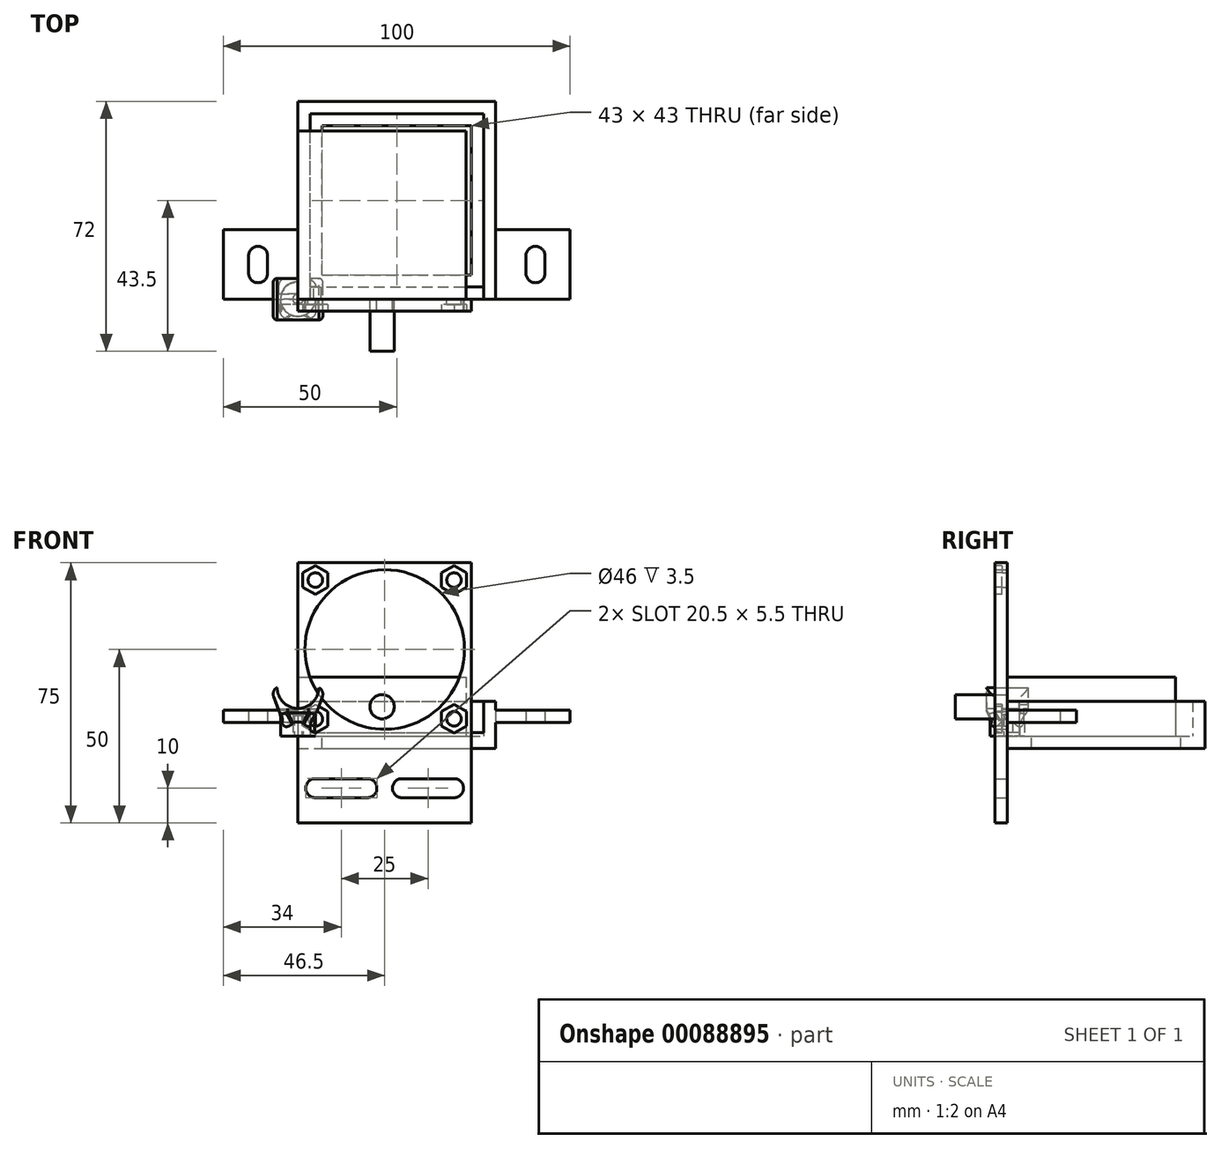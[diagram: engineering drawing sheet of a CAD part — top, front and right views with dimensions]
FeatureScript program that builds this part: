
annotation { "Feature Type Name" : "Feature", "Feature Type Description" : "" }
export const myFeature = defineFeature(function(context is Context, id is Id, definition is map)
    precondition{}
    {
        {
            var Q0;
            Q0=qCreatedBy(makeId("Top.planeOp"),FACE);
            var sketch = newSketch(context, id + "F0", { "sketchPlane" : qUnion([Q0])});
            skCircle(sketch, "E0", {"center": v(0, 0) * mm, "radius": 5 * mm});
            skArc(sketch, "E1", {"start": v(1.12, -1) * mm, "mid": v(0, 1.5) * mm, "end": v(-1.12, -1) * mm});
            skLineSegment(sketch, "E2", {"start": v(-1.12, -1) * mm, "end": v(1.12, -1) * mm});
            skSolve(sketch);
        }
        {
            var Q0;
            Q0 = qSketchRegion(id + "F0", true);
            extrude(context, id + "F1", {"entities" : qUnion([Q0]), "depth" : 6 * mm});
        }
        {
            var Q0;
            Q0=qCreatedBy(makeId("Front.planeOp"),FACE);
            var sketch = newSketch(context, id + "F2", { "sketchPlane" : qUnion([Q0])});
            skArc(sketch, "E3", {"start": v(-6, 14) * mm, "mid": v(0, 8) * mm, "end": v(6, 14) * mm});
            skLineSegment(sketch, "E4", {"start": v(0, 43.04) * mm, "end": v(0, -18.68) * mm, "construction": true});
            skLineSegment(sketch, "E5", {"start": v(8, 14) * mm, "end": v(6, 14) * mm});
            skLineSegment(sketch, "E6.trimOffspring", {"start": v(-6, 14) * mm, "end": v(-8, 14) * mm});
            skLineSegment(sketch, "E7", {"start": v(8, 14) * mm, "end": v(5, 6) * mm});
            skLineSegment(sketch, "E8", {"start": v(5, 6) * mm, "end": v(-5, 6) * mm});
            skLineSegment(sketch, "E9", {"start": v(-5, 6) * mm, "end": v(-8, 14) * mm});
            skSolve(sketch);
        }
        {
            var Q0;
            Q0 = qSketchRegion(id + "F2", true);
            extrude(context, id + "F3", {"entities" : qUnion([Q0]), "operationType" : NewBodyOperationType.ADD, "endBound" : BoundingType.SYMMETRIC, "depth" : 12 * mm});
        }
        {
            var Q0;
            Q0=makeQuery(id+"F3.opExtrude","CAP_EDGE",EDGE,{"disambiguationData":[OSD([sQuery(id+"F2.wireOp",EDGE,"E7")])],"isStart":false});
            var Q1;
            Q1=makeQuery(id+"F3.opExtrude","CAP_EDGE",EDGE,{"disambiguationData":[OSD([sQuery(id+"F2.wireOp",EDGE,"E9")])],"isStart":false});
            var Q2;
            Q2=makeQuery(id+"F3.opExtrude","CAP_EDGE",EDGE,{"disambiguationData":[OSD([sQuery(id+"F2.wireOp",EDGE,"E9")])],"isStart":true});
            var Q3;
            Q3=makeQuery(id+"F3.opExtrude","CAP_EDGE",EDGE,{"disambiguationData":[OSD([sQuery(id+"F2.wireOp",EDGE,"E7")])],"isStart":true});
            var Q4;
            Q4=makeQuery(id+"F3.opExtrude","SWEPT_EDGE",EDGE,{"disambiguationData":[OSD([sQuery(id+"F2.wireOp",EDGE,"E5"),sQuery(id+"F2.wireOp",EDGE,"E7")])]});
            var Q5;
            Q5=makeQuery(id+"F3.opExtrude","SWEPT_EDGE",EDGE,{"disambiguationData":[OSD([sQuery(id+"F2.wireOp",EDGE,"E6.trimOffspring"),sQuery(id+"F2.wireOp",EDGE,"E9")])]});
            var Q6;
            {var subQ0=sQuery(id+"F2.wireOp",EDGE,"E9");var subQ1=sQuery(id+"F2.wireOp",EDGE,"E8");Q6=makeQuery(id+"F3.boolean.opBoolean","SPLIT",EDGE,{"disambiguationData":[TD([makeQuery(id+"F3.opExtrude","CAP_FACE",FACE,{"disambiguationData":[OSD([sQuery(id+"F2.wireOp",EDGE,"E3"),sQuery(id+"F2.wireOp",EDGE,"E5"),sQuery(id+"F2.wireOp",EDGE,"E6.trimOffspring"),sQuery(id+"F2.wireOp",EDGE,"E7"),subQ1,subQ0])],"isStart":false})])],"derivedFrom":makeQuery(id+"F3.opExtrude","SWEPT_EDGE",EDGE,{"disambiguationData":[OSD([subQ1,subQ0])]})});}
            var Q7;
            Q7=makeQuery(id+"F3.opExtrude","CAP_EDGE",EDGE,{"disambiguationData":[OSD([sQuery(id+"F2.wireOp",EDGE,"E8")])],"isStart":true});
            var Q8;
            {var subQ0=sQuery(id+"F2.wireOp",EDGE,"E8");var subQ1=sQuery(id+"F2.wireOp",EDGE,"E7");Q8=makeQuery(id+"F3.boolean.opBoolean","SPLIT",EDGE,{"disambiguationData":[TD([makeQuery(id+"F3.opExtrude","CAP_FACE",FACE,{"disambiguationData":[OSD([sQuery(id+"F2.wireOp",EDGE,"E3"),sQuery(id+"F2.wireOp",EDGE,"E5"),sQuery(id+"F2.wireOp",EDGE,"E6.trimOffspring"),subQ1,subQ0,sQuery(id+"F2.wireOp",EDGE,"E9")])],"isStart":true})])],"derivedFrom":makeQuery(id+"F3.opExtrude","SWEPT_EDGE",EDGE,{"disambiguationData":[OSD([subQ1,subQ0])]})});}
            var Q9;
            {var subQ0=sQuery(id+"F2.wireOp",EDGE,"E8");var subQ1=sQuery(id+"F2.wireOp",EDGE,"E7");Q9=makeQuery(id+"F3.boolean.opBoolean","SPLIT",EDGE,{"disambiguationData":[TD([makeQuery(id+"F3.opExtrude","CAP_FACE",FACE,{"disambiguationData":[OSD([sQuery(id+"F2.wireOp",EDGE,"E3"),sQuery(id+"F2.wireOp",EDGE,"E5"),sQuery(id+"F2.wireOp",EDGE,"E6.trimOffspring"),subQ1,subQ0,sQuery(id+"F2.wireOp",EDGE,"E9")])],"isStart":false})])],"derivedFrom":makeQuery(id+"F3.opExtrude","SWEPT_EDGE",EDGE,{"disambiguationData":[OSD([subQ1,subQ0])]})});}
            var Q10;
            Q10=makeQuery(id+"F3.opExtrude","CAP_EDGE",EDGE,{"disambiguationData":[OSD([sQuery(id+"F2.wireOp",EDGE,"E8")])],"isStart":false});
            fillet(context, id + "F4", {"entities" : qUnion([Q0, Q1, Q2, Q3, Q4, Q5, Q6, Q7, Q8, Q9, Q10]), "radius" : 2 * mm, "tangentPropagation" : true, "allowEdgeOverflow" : false});
        }
        {
            var Q0;
            Q0=makeQuery(id+"F4.opFillet","BLEND_EDGE",EDGE,{"blendedFrom":[makeQuery(id+"F3.opExtrude","CAP_EDGE",EDGE,{"disambiguationData":[OSD([sQuery(id+"F2.wireOp",EDGE,"E8")])],"isStart":false}),makeQuery(id+"F1.opExtrude","SWEPT_FACE",FACE,{"disambiguationData":[OSD([sQuery(id+"F0.wireOp",EDGE,"E0")])]})],"blendedInto":[makeQuery(id+"F1.opExtrude","SWEPT_FACE",FACE,{"disambiguationData":[OSD([sQuery(id+"F0.wireOp",EDGE,"E0")])]})]});
            fillet(context, id + "F5", {"entities" : qUnion([Q0]), "radius" : 5 * mm, "tangentPropagation" : true, "allowEdgeOverflow" : false});
        }
        {
            var Q0;
            Q0=qCreatedBy(makeId("Right.planeOp"),FACE);
            var sketch = newSketch(context, id + "F6", { "sketchPlane" : qUnion([Q0])});
            skLineSegment(sketch, "E10.bottom", {"start": v(-1.5, 7.75) * mm, "end": v(1.5, 7.75) * mm});
            skLineSegment(sketch, "E10.top", {"start": v(-1.5, 6.25) * mm, "end": v(1.5, 6.25) * mm});
            skLineSegment(sketch, "E10.left", {"start": v(-1.5, 7.75) * mm, "end": v(-1.5, 6.25) * mm});
            skLineSegment(sketch, "E10.right", {"start": v(1.5, 7.75) * mm, "end": v(1.5, 6.25) * mm});
            skSolve(sketch);
        }
        {
            var Q0;
            Q0 = qSketchRegion(id + "F6", true);
            extrude(context, id + "F7", {"entities" : qUnion([Q0]), "operationType" : NewBodyOperationType.REMOVE, "endBound" : BoundingType.SYMMETRIC, "depth" : 100 * mm});
        }
        {
            var Q0;
            Q0=qCreatedBy(makeId("Top.planeOp"),FACE);
            var sketch = newSketch(context, id + "F8", { "sketchPlane" : qUnion([Q0])});
            skLineSegment(sketch, "E11.bottom", {"start": v(0, 0) * mm, "end": v(57, 0) * mm});
            skLineSegment(sketch, "E11.top", {"start": v(0, 57) * mm, "end": v(57, 57) * mm});
            skLineSegment(sketch, "E11.left", {"start": v(0, 0) * mm, "end": v(0, 57) * mm});
            skLineSegment(sketch, "E11.right", {"start": v(57, 0) * mm, "end": v(57, 57) * mm});
            skLineSegment(sketch, "E12.bottom", {"start": v(3.5, 3.5) * mm, "end": v(53.5, 3.5) * mm});
            skLineSegment(sketch, "E12.top", {"start": v(3.5, 53.5) * mm, "end": v(53.5, 53.5) * mm});
            skLineSegment(sketch, "E12.left", {"start": v(3.5, 3.5) * mm, "end": v(3.5, 53.5) * mm});
            skLineSegment(sketch, "E12.right", {"start": v(53.5, 3.5) * mm, "end": v(53.5, 53.5) * mm});
            skLineSegment(sketch, "E13", {"start": v(0, 0) * mm, "end": v(57, 57) * mm, "construction": true});
            skPoint(sketch, "E14", {"position": v(28.5, 28.5) * mm});
            skLineSegment(sketch, "E15", {"start": v(3.5, 53.5) * mm, "end": v(53.5, 3.5) * mm, "construction": true});
            skLineSegment(sketch, "E16", {"start": v(3.5, 3.5) * mm, "end": v(53.5, 53.5) * mm, "construction": true});
            skSolve(sketch);
        }
        {
            var Q0;
            Q0 = qSketchRegion(id + "F8", true);
            extrude(context, id + "F9", {"entities" : qUnion([Q0]), "depth" : 10 * mm});
        }
        {
            var Q0;
            Q0=makeQuery(id+"F9.opExtrude","CAP_FACE",FACE,{"disambiguationData":[OSD([sQuery(id+"F8.wireOp",EDGE,"E11.bottom"),sQuery(id+"F8.wireOp",EDGE,"E11.top"),sQuery(id+"F8.wireOp",EDGE,"E11.left"),sQuery(id+"F8.wireOp",EDGE,"E11.right"),sQuery(id+"F8.wireOp",EDGE,"E12.bottom"),sQuery(id+"F8.wireOp",EDGE,"E12.top"),sQuery(id+"F8.wireOp",EDGE,"E12.left"),sQuery(id+"F8.wireOp",EDGE,"E12.right")])],"isStart":true});
            var sketch = newSketch(context, id + "F10", { "sketchPlane" : qUnion([Q0])});
            skLineSegment(sketch, "E17.0", {"start": v(0, 0) * mm, "end": v(0, -57) * mm});
            skLineSegment(sketch, "E17.1", {"start": v(0, -57) * mm, "end": v(57, -57) * mm});
            skLineSegment(sketch, "E17.2", {"start": v(57, 0) * mm, "end": v(57, -57) * mm});
            skLineSegment(sketch, "E17.3", {"start": v(0, 0) * mm, "end": v(57, 0) * mm});
            skLineSegment(sketch, "E18.0", {"start": v(7, -50) * mm, "end": v(50, -50) * mm});
            skLineSegment(sketch, "E18.1", {"start": v(7, -7) * mm, "end": v(7, -50) * mm});
            skLineSegment(sketch, "E18.2", {"start": v(7, -7) * mm, "end": v(50, -7) * mm});
            skLineSegment(sketch, "E18.3", {"start": v(50, -7) * mm, "end": v(50, -50) * mm});
            skSolve(sketch);
        }
        {
            var Q0;
            Q0 = qSketchRegion(id + "F10", true);
            extrude(context, id + "F11", {"entities" : qUnion([Q0]), "operationType" : NewBodyOperationType.ADD, "depth" : 3.5 * mm});
        }
        {
            var Q0;
            Q0=makeQuery(id+"F11.boolean.opBoolean","MERGE",FACE,{"derivedFrom":[makeQuery(id+"F9.opExtrude","SWEPT_FACE",FACE,{"disambiguationData":[OSD([sQuery(id+"F8.wireOp",EDGE,"E11.bottom")])]}),makeQuery(id+"F11.opExtrude","SWEPT_FACE",FACE,{"disambiguationData":[OSD([sQuery(id+"F10.wireOp",EDGE,"E17.3")])]})]});
            var sketch = newSketch(context, id + "F12", { "sketchPlane" : qUnion([Q0])});
            skLineSegment(sketch, "E19.bottom", {"start": v(3.5, 10) * mm, "end": v(53.5, 10) * mm});
            skLineSegment(sketch, "E19.top", {"start": v(3.5, 1) * mm, "end": v(53.5, 1) * mm});
            skLineSegment(sketch, "E19.left", {"start": v(3.5, 10) * mm, "end": v(3.5, 1) * mm});
            skLineSegment(sketch, "E19.right", {"start": v(53.5, 10) * mm, "end": v(53.5, 1) * mm});
            skSolve(sketch);
        }
        {
            var Q0;
            Q0 = qSketchRegion(id + "F12", true);
            var Q1;
            Q1=makeQuery(id+"F9.opExtrude","SWEPT_FACE",FACE,{"disambiguationData":[OSD([sQuery(id+"F8.wireOp",EDGE,"E12.bottom")])]});
            extrude(context, id + "F13", {"entities" : qUnion([Q0]), "operationType" : NewBodyOperationType.REMOVE, "endBound" : BoundingType.UP_TO_SURFACE, "oppositeDirection" : true, "endBoundEntityFace" : qUnion([Q1]), "depth" : 25 * mm});
        }
        {
            var Q0;
            Q0=qCreatedBy(makeId("Top.planeOp"),FACE);
            cPlane(context, id + "F14", {"entities" : qUnion([Q0]), "cplaneType" : CPlaneType.OFFSET, "offset" : 17 * mm, "width" : 150 * mm, "height" : 150 * mm});
        }
        {
            var Q0;
            Q0=qCreatedBy(id+"F14.planeOp",FACE);
            cPlane(context, id + "F15", {"entities" : qUnion([Q0]), "cplaneType" : CPlaneType.OFFSET, "offset" : 13 * mm, "oppositeDirection" : true, "width" : 150 * mm, "height" : 150 * mm});
        }
        {
            var Q0;
            Q0=qCreatedBy(id+"F15.planeOp",FACE);
            var sketch = newSketch(context, id + "F16", { "sketchPlane" : qUnion([Q0])});
            skLineSegment(sketch, "E20.bottom", {"start": v(78.5, 0) * mm, "end": v(57, 0) * mm});
            skLineSegment(sketch, "E20.top", {"start": v(78.5, 20) * mm, "end": v(57, 20) * mm});
            skLineSegment(sketch, "E20.left", {"start": v(78.5, 0) * mm, "end": v(78.5, 20) * mm});
            skLineSegment(sketch, "E20.right", {"start": v(57, 0) * mm, "end": v(57, 20) * mm});
            skLineSegment(sketch, "E21", {"start": v(28.5, -59.7) * mm, "end": v(28.5, 78.18) * mm, "construction": true});
            skLineSegment(sketch, "E22", {"start": v(68.5, -81.78) * mm, "end": v(68.5, 92.7) * mm, "construction": true});
            skLineSegment(sketch, "E23.MirrorCS", {"start": v(-11.5, -81.78) * mm, "end": v(-11.5, 92.7) * mm, "construction": true});
            skArc(sketch, "E24", {"start": v(71.25, 12.5) * mm, "mid": v(68.5, 15.25) * mm, "end": v(65.75, 12.5) * mm});
            skLineSegment(sketch, "E25", {"start": v(85.64, 10) * mm, "end": v(47.44, 10) * mm, "construction": true});
            skLineSegment(sketch, "E26", {"start": v(71.25, 12.5) * mm, "end": v(71.25, 10) * mm});
            skLineSegment(sketch, "E27", {"start": v(65.75, 12.5) * mm, "end": v(65.75, 10) * mm});
            skArc(sketch, "E28.MirrorCS", {"start": v(71.25, 7.5) * mm, "mid": v(68.5, 4.75) * mm, "end": v(65.75, 7.5) * mm});
            skLineSegment(sketch, "E29.MirrorCS", {"start": v(71.25, 7.5) * mm, "end": v(71.25, 10) * mm});
            skLineSegment(sketch, "E30.MirrorCS", {"start": v(65.75, 7.5) * mm, "end": v(65.75, 10) * mm});
            skLineSegment(sketch, "E31.MirrorCS", {"start": v(57, 20) * mm, "end": v(57, 0) * mm});
            skLineSegment(sketch, "E32.MirrorCS", {"start": v(78.5, 20) * mm, "end": v(78.5, 0) * mm});
            skLineSegment(sketch, "E33.MirrorCS", {"start": v(28.5, 79.7) * mm, "end": v(28.5, -58.18) * mm, "construction": true});
            skLineSegment(sketch, "E34.MirrorCS", {"start": v(-14.25, 7.5) * mm, "end": v(-14.25, 10) * mm});
            skLineSegment(sketch, "E35.MirrorCS", {"start": v(-8.75, 7.5) * mm, "end": v(-8.75, 10) * mm});
            skLineSegment(sketch, "E36.MirrorCS", {"start": v(-14.25, 12.5) * mm, "end": v(-14.25, 10) * mm});
            skLineSegment(sketch, "E37.MirrorCS", {"start": v(-8.75, 12.5) * mm, "end": v(-8.75, 10) * mm});
            skArc(sketch, "E38.MirrorCS", {"start": v(-14.25, 7.5) * mm, "mid": v(-11.5, 4.75) * mm, "end": v(-8.75, 7.5) * mm});
            skLineSegment(sketch, "E39.MirrorCS", {"start": v(-21.5, 20) * mm, "end": v(-21.5, 0) * mm});
            skLineSegment(sketch, "E40.MirrorCS", {"start": v(-21.5, 0) * mm, "end": v(0, 0) * mm});
            skArc(sketch, "E41.MirrorCS", {"start": v(-14.25, 12.5) * mm, "mid": v(-11.5, 15.25) * mm, "end": v(-8.75, 12.5) * mm});
            skLineSegment(sketch, "E42.MirrorCS", {"start": v(-21.5, 20) * mm, "end": v(0, 20) * mm});
            skLineSegment(sketch, "E43.MirrorCS", {"start": v(0, 0) * mm, "end": v(0, 20) * mm});
            skLineSegment(sketch, "E44.MirrorCS", {"start": v(-21.5, 0) * mm, "end": v(-21.5, 20) * mm});
            skLineSegment(sketch, "E45.MirrorCS", {"start": v(0, 20) * mm, "end": v(0, 0) * mm});
            skSolve(sketch);
        }
        {
            var Q0;
            Q0 = qSketchRegion(id + "F16", true);
            extrude(context, id + "F17", {"entities" : qUnion([Q0]), "operationType" : NewBodyOperationType.ADD, "depth" : 3.5 * mm});
        }
        {
            var Q0;
            Q0=qCreatedBy(makeId("Top.planeOp"),FACE);
            var sketch = newSketch(context, id + "F18", { "sketchPlane" : qUnion([Q0])});
            skLineSegment(sketch, "E46.bottom", {"start": v(0, 0) * mm, "end": v(48.5, 0) * mm});
            skLineSegment(sketch, "E46.top", {"start": v(0, 48.5) * mm, "end": v(48.5, 48.5) * mm});
            skLineSegment(sketch, "E46.left", {"start": v(0, 0) * mm, "end": v(0, 48.5) * mm});
            skLineSegment(sketch, "E46.right", {"start": v(48.5, 0) * mm, "end": v(48.5, 48.5) * mm});
            skSolve(sketch);
        }
        {
            var Q0;
            Q0 = qSketchRegion(id + "F18", true);
            extrude(context, id + "F19", {"entities" : qUnion([Q0]), "depth" : 17 * mm});
        }
        {
            var Q0;
            Q0=makeQuery(id+"F19.opExtrude","SWEPT_FACE",FACE,{"disambiguationData":[OSD([sQuery(id+"F18.wireOp",EDGE,"E46.bottom")])]});
            var sketch = newSketch(context, id + "F20", { "sketchPlane" : qUnion([Q0])});
            skCircle(sketch, "E47", {"center": v(24.25, 8.5) * mm, "radius": 3.5 * mm});
            skLineSegment(sketch, "E48", {"start": v(0, 0) * mm, "end": v(48.5, 17) * mm, "construction": true});
            skLineSegment(sketch, "E49", {"start": v(48.5, 0) * mm, "end": v(0, 17) * mm, "construction": true});
            skSolve(sketch);
        }
        {
            var Q0;
            Q0 = qSketchRegion(id + "F20", true);
            extrude(context, id + "F21", {"entities" : qUnion([Q0]), "operationType" : NewBodyOperationType.ADD, "depth" : 15 * mm});
        }
        {
            var Q0;
            Q0=qCreatedBy(makeId("Front.planeOp"),FACE);
            var sketch = newSketch(context, id + "F22", { "sketchPlane" : qUnion([Q0])});
            skLineSegment(sketch, "E50.bottom", {"start": v(0, 0) * mm, "end": v(50, 0) * mm});
            skLineSegment(sketch, "E50.top", {"start": v(0, 50) * mm, "end": v(50, 50) * mm});
            skLineSegment(sketch, "E50.left", {"start": v(0, 0) * mm, "end": v(0, 50) * mm});
            skLineSegment(sketch, "E50.right", {"start": v(50, 0) * mm, "end": v(50, 50) * mm});
            skCircle(sketch, "E51", {"center": v(5, 45) * mm, "radius": 2.1 * mm});
            skLineSegment(sketch, "E52", {"start": v(25, 60.25) * mm, "end": v(25, -23.6) * mm, "construction": true});
            skCircle(sketch, "E53.MirrorC", {"center": v(45, 45) * mm, "radius": 2.1 * mm});
            skLineSegment(sketch, "E54", {"start": v(-16.82, 25) * mm, "end": v(85.55, 25) * mm, "construction": true});
            skCircle(sketch, "E55.MirrorC", {"center": v(5, 5) * mm, "radius": 2.1 * mm});
            skCircle(sketch, "E56.MirrorC", {"center": v(45, 5) * mm, "radius": 2.1 * mm});
            skCircle(sketch, "E57", {"center": v(25, 25) * mm, "radius": 23 * mm});
            skLineSegment(sketch, "E58.top", {"start": v(0, -25) * mm, "end": v(50, -25) * mm});
            skLineSegment(sketch, "E58.left", {"start": v(0, 0) * mm, "end": v(0, -25) * mm});
            skLineSegment(sketch, "E58.right", {"start": v(50, 0) * mm, "end": v(50, -25) * mm});
            skLineSegment(sketch, "E59", {"start": v(-29.3, -15) * mm, "end": v(102.52, -15) * mm, "construction": true});
            skArc(sketch, "E60", {"start": v(5, -12.25) * mm, "mid": v(2.25, -15) * mm, "end": v(5, -17.75) * mm});
            skArc(sketch, "E61", {"start": v(20, -17.75) * mm, "mid": v(22.75, -15) * mm, "end": v(20, -12.25) * mm});
            skLineSegment(sketch, "E62", {"start": v(-14.1, -5) * mm, "end": v(96.5, -5) * mm, "construction": true});
            skLineSegment(sketch, "E63", {"start": v(5, -12.25) * mm, "end": v(20, -12.25) * mm});
            skLineSegment(sketch, "E64", {"start": v(20, -17.75) * mm, "end": v(5, -17.75) * mm});
            skLineSegment(sketch, "E65", {"start": v(12.5, -50.27) * mm, "end": v(12.5, -8.77) * mm, "construction": true});
            skLineSegment(sketch, "E66.MirrorCS", {"start": v(30, -17.75) * mm, "end": v(45, -17.75) * mm});
            skLineSegment(sketch, "E67.MirrorCS", {"start": v(45, -12.25) * mm, "end": v(30, -12.25) * mm});
            skArc(sketch, "E68.MirrorCS", {"start": v(30, -17.75) * mm, "mid": v(27.25, -15) * mm, "end": v(30, -12.25) * mm});
            skArc(sketch, "E69.MirrorCS", {"start": v(45, -12.25) * mm, "mid": v(47.75, -15) * mm, "end": v(45, -17.75) * mm});
            skSolve(sketch);
        }
        {
            var Q0;
            Q0 = qSketchRegion(id + "F22", true);
            extrude(context, id + "F23", {"entities" : qUnion([Q0]), "depth" : 3.5 * mm});
        }
        {
            var Q0;
            Q0=makeQuery(id+"F23.opExtrude","CAP_FACE",FACE,{"disambiguationData":[OSD([sQuery(id+"F22.wireOp",EDGE,"E50.top"),sQuery(id+"F22.wireOp",EDGE,"E50.left"),sQuery(id+"F22.wireOp",EDGE,"E50.right"),sQuery(id+"F22.wireOp",EDGE,"E51"),sQuery(id+"F22.wireOp",EDGE,"E53.MirrorC"),sQuery(id+"F22.wireOp",EDGE,"E55.MirrorC"),sQuery(id+"F22.wireOp",EDGE,"E56.MirrorC"),sQuery(id+"F22.wireOp",EDGE,"E57"),sQuery(id+"F22.wireOp",EDGE,"E58.top"),sQuery(id+"F22.wireOp",EDGE,"E58.left"),sQuery(id+"F22.wireOp",EDGE,"E58.right"),sQuery(id+"F22.wireOp",EDGE,"E60"),sQuery(id+"F22.wireOp",EDGE,"E61"),sQuery(id+"F22.wireOp",EDGE,"E63"),sQuery(id+"F22.wireOp",EDGE,"E64"),sQuery(id+"F22.wireOp",EDGE,"E66.MirrorCS"),sQuery(id+"F22.wireOp",EDGE,"E67.MirrorCS"),sQuery(id+"F22.wireOp",EDGE,"E68.MirrorCS"),sQuery(id+"F22.wireOp",EDGE,"E69.MirrorCS")])],"isStart":false});
            var sketch = newSketch(context, id + "F24", { "sketchPlane" : qUnion([Q0])});
            skCircle(sketch, "E70.cCircle", {"center": v(5, 45) * mm, "radius": 3.6 * mm, "construction": true});
            skLineSegment(sketch, "E70.0", {"start": v(1.4, 42.92) * mm, "end": v(1.4, 47.08) * mm});
            skLineSegment(sketch, "E70.1", {"start": v(1.4, 47.08) * mm, "end": v(5, 49.16) * mm});
            skLineSegment(sketch, "E70.2", {"start": v(5, 49.16) * mm, "end": v(8.6, 47.08) * mm});
            skLineSegment(sketch, "E70.3", {"start": v(8.6, 47.08) * mm, "end": v(8.6, 42.92) * mm});
            skLineSegment(sketch, "E70.4", {"start": v(8.6, 42.92) * mm, "end": v(5, 40.84) * mm});
            skLineSegment(sketch, "E70.5", {"start": v(5, 40.84) * mm, "end": v(1.4, 42.92) * mm});
            skPoint(sketch, "E70.0.midPoint", {"position": v(1.4, 45) * mm});
            skCircle(sketch, "E71.cCircle", {"center": v(45, 45) * mm, "radius": 3.6 * mm, "construction": true});
            skLineSegment(sketch, "E71.0", {"start": v(41.4, 42.92) * mm, "end": v(41.4, 47.08) * mm});
            skLineSegment(sketch, "E71.1", {"start": v(41.4, 47.08) * mm, "end": v(45, 49.16) * mm});
            skLineSegment(sketch, "E71.2", {"start": v(45, 49.16) * mm, "end": v(48.6, 47.08) * mm});
            skLineSegment(sketch, "E71.3", {"start": v(48.6, 47.08) * mm, "end": v(48.6, 42.92) * mm});
            skLineSegment(sketch, "E71.4", {"start": v(48.6, 42.92) * mm, "end": v(45, 40.84) * mm});
            skLineSegment(sketch, "E71.5", {"start": v(45, 40.84) * mm, "end": v(41.4, 42.92) * mm});
            skPoint(sketch, "E71.0.midPoint", {"position": v(41.4, 45) * mm});
            skCircle(sketch, "E72.cCircle", {"center": v(45, 5) * mm, "radius": 3.6 * mm, "construction": true});
            skLineSegment(sketch, "E72.0", {"start": v(41.4, 2.92) * mm, "end": v(41.4, 7.08) * mm});
            skLineSegment(sketch, "E72.1", {"start": v(41.4, 7.08) * mm, "end": v(45, 9.16) * mm});
            skLineSegment(sketch, "E72.2", {"start": v(45, 9.16) * mm, "end": v(48.6, 7.08) * mm});
            skLineSegment(sketch, "E72.3", {"start": v(48.6, 7.08) * mm, "end": v(48.6, 2.92) * mm});
            skLineSegment(sketch, "E72.4", {"start": v(48.6, 2.92) * mm, "end": v(45, 0.84) * mm});
            skLineSegment(sketch, "E72.5", {"start": v(45, 0.84) * mm, "end": v(41.4, 2.92) * mm});
            skPoint(sketch, "E72.0.midPoint", {"position": v(41.4, 5) * mm});
            skCircle(sketch, "E73.cCircle", {"center": v(5, 5) * mm, "radius": 3.6 * mm, "construction": true});
            skLineSegment(sketch, "E73.0", {"start": v(1.4, 7.08) * mm, "end": v(5, 9.16) * mm});
            skLineSegment(sketch, "E73.1", {"start": v(5, 9.16) * mm, "end": v(8.6, 7.08) * mm});
            skLineSegment(sketch, "E73.2", {"start": v(8.6, 7.08) * mm, "end": v(8.6, 2.92) * mm});
            skLineSegment(sketch, "E73.3", {"start": v(8.6, 2.92) * mm, "end": v(5, 0.84) * mm});
            skLineSegment(sketch, "E73.4", {"start": v(5, 0.84) * mm, "end": v(1.4, 2.92) * mm});
            skLineSegment(sketch, "E73.5", {"start": v(1.4, 2.92) * mm, "end": v(1.4, 7.08) * mm});
            skPoint(sketch, "E73.0.midPoint", {"position": v(3.2, 8.12) * mm});
            skSolve(sketch);
        }
        {
            var Q0;
            Q0 = qSketchRegion(id + "F24", true);
            extrude(context, id + "F25", {"entities" : qUnion([Q0]), "operationType" : NewBodyOperationType.REMOVE, "oppositeDirection" : true, "depth" : 2 * mm});
        }
    });
